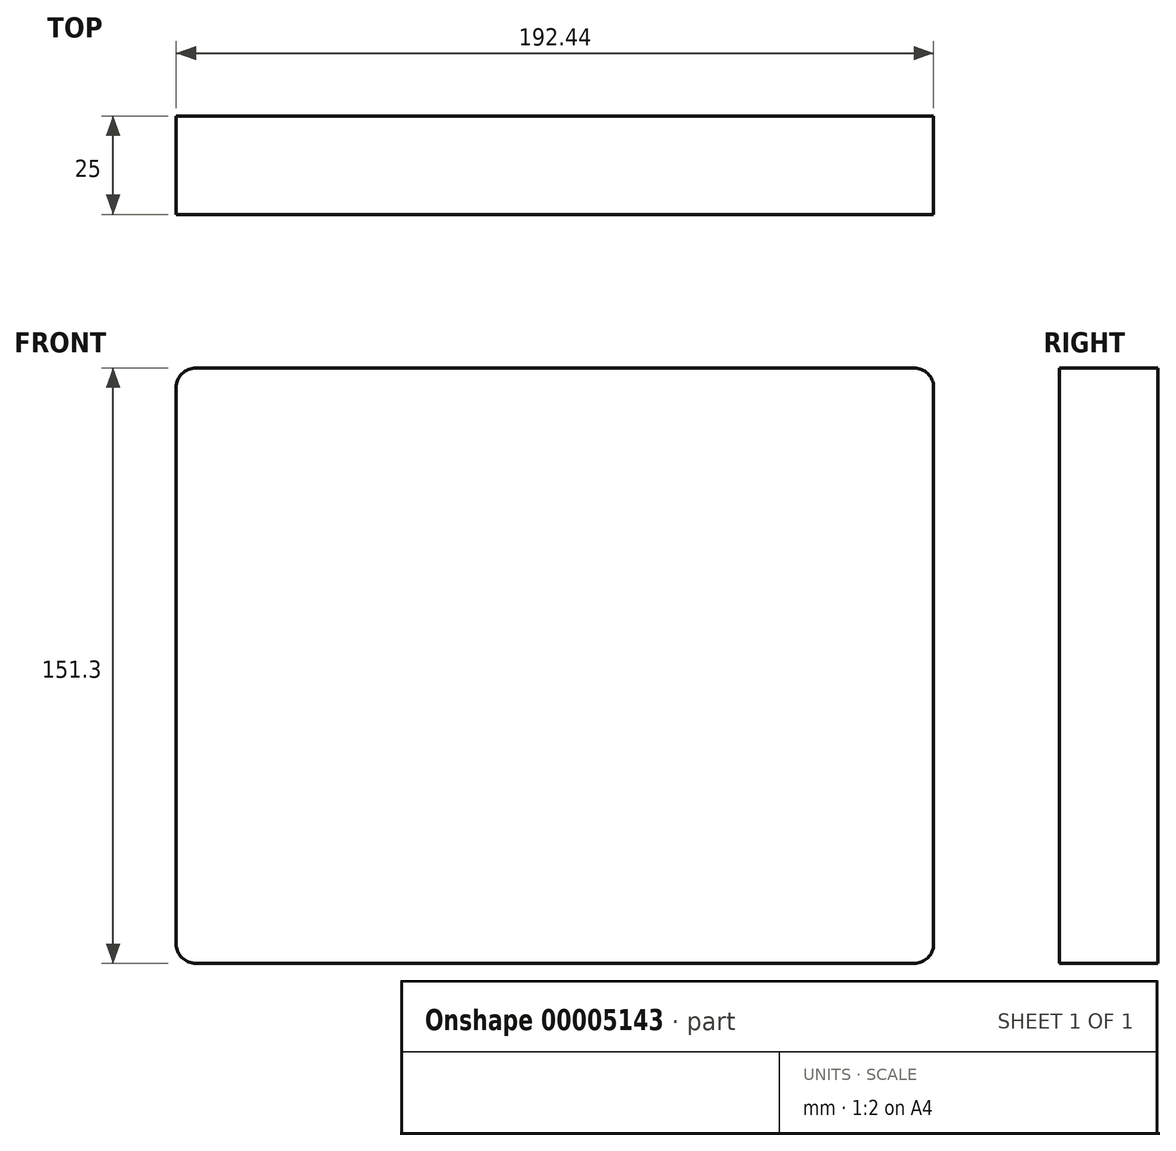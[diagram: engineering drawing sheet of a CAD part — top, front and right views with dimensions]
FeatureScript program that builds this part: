
annotation { "Feature Type Name" : "Feature", "Feature Type Description" : "" }
export const myFeature = defineFeature(function(context is Context, id is Id, definition is map)
    precondition{}
    {
        {
            var Q0;
            Q0=qCreatedBy(makeId("Front.planeOp"),FACE);
            var sketch = newSketch(context, id + "F0", { "sketchPlane" : qUnion([Q0])});
            skLineSegment(sketch, "E0.rect.bottom", {"start": v(91.22, 75.65) * mm, "end": v(-91.22, 75.65) * mm});
            skLineSegment(sketch, "E0.rect.top", {"start": v(91.22, -75.65) * mm, "end": v(-91.22, -75.65) * mm});
            skLineSegment(sketch, "E0.rect.left", {"start": v(96.22, 70.65) * mm, "end": v(96.22, -70.65) * mm});
            skLineSegment(sketch, "E0.rect.right", {"start": v(-96.22, 70.65) * mm, "end": v(-96.22, -70.65) * mm});
            skPoint(sketch, "E0.rect.middle", {"position": v(0, 0) * mm});
            skPoint(sketch, "E1.visualSharp", {"position": v(-96.22, 75.65) * mm});
            skArc(sketch, "E1.filletArc", {"start": v(-91.22, 75.65) * mm, "mid": v(-94.75, 74.19) * mm, "end": v(-96.22, 70.65) * mm});
            skPoint(sketch, "E2.visualSharp", {"position": v(96.22, 75.65) * mm});
            skArc(sketch, "E2.filletArc", {"start": v(96.22, 70.65) * mm, "mid": v(94.75, 74.19) * mm, "end": v(91.22, 75.65) * mm});
            skPoint(sketch, "E3.visualSharp", {"position": v(96.22, -75.65) * mm});
            skArc(sketch, "E3.filletArc", {"start": v(91.22, -75.65) * mm, "mid": v(94.75, -74.19) * mm, "end": v(96.22, -70.65) * mm});
            skPoint(sketch, "E4.visualSharp", {"position": v(-96.22, -75.65) * mm});
            skArc(sketch, "E4.filletArc", {"start": v(-96.22, -70.65) * mm, "mid": v(-94.75, -74.19) * mm, "end": v(-91.22, -75.65) * mm});
            skSolve(sketch);
        }
        {
            var Q0;
            Q0=makeQuery(id+"F0.imprint","IMPRINT",FACE,{"disambiguationData":[TD([[makeQuery(id+"F0.imprint","IMPRINT",EDGE,{"derivedFrom":sQuery(id+"F0.wireOp",EDGE,"E0.rect.bottom")}),1.0]])]});
            extrude(context, id + "F1", {"entities" : qUnion([Q0]), "depth" : 25 * mm});
        }
    });
